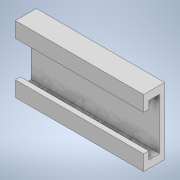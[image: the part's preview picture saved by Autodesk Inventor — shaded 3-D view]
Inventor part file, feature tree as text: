
AUTODESK INVENTOR PART (.ipt)
format: ipt  version: 2021 (Build 250183000, 183)  size: 142,336 bytes
history: native  units: in
note: dims shown in document units (in); Inventor stores cm internally (conversion verified against a paired STEP export)
features: extrude x4, sketch x4
ambient origin geometry x8: Origin, YZ Plane, XZ Plane, XY Plane, X Axis, Y Axis, Z Axis, Center Point
bodies: Solid1 (feature_tree)
feature tree (8):
  extrude  "Extrusion1"  Depth=5.1181in
  extrude  "Extrusion2"  Depth=0.5906in
  extrude  "Extrusion3"  Depth=0.8268in TaperAngle=0.0deg
  extrude  "Extrusion4"  Depth=1.1811in
  sketch  "Sketch1"  dims[d0=9.8425in d1=5.1181in]
  sketch  "Sketch2"  dims[d2=0.3937in d3=0.0in d4=0.5906in]
  sketch  "Sketch3"  dims[d5=0.5906in d6=0.8268in d7=0.0in]
  sketch  "Sketch4"  dims[d8=1.1811in d9=1.1811in d10=0.3937in d11=0.0in d12=0.1969in d13=0.3937in d14=0.3937in d15=0.0in d16=0.0in d17=0.7874in d18=0.0in]
